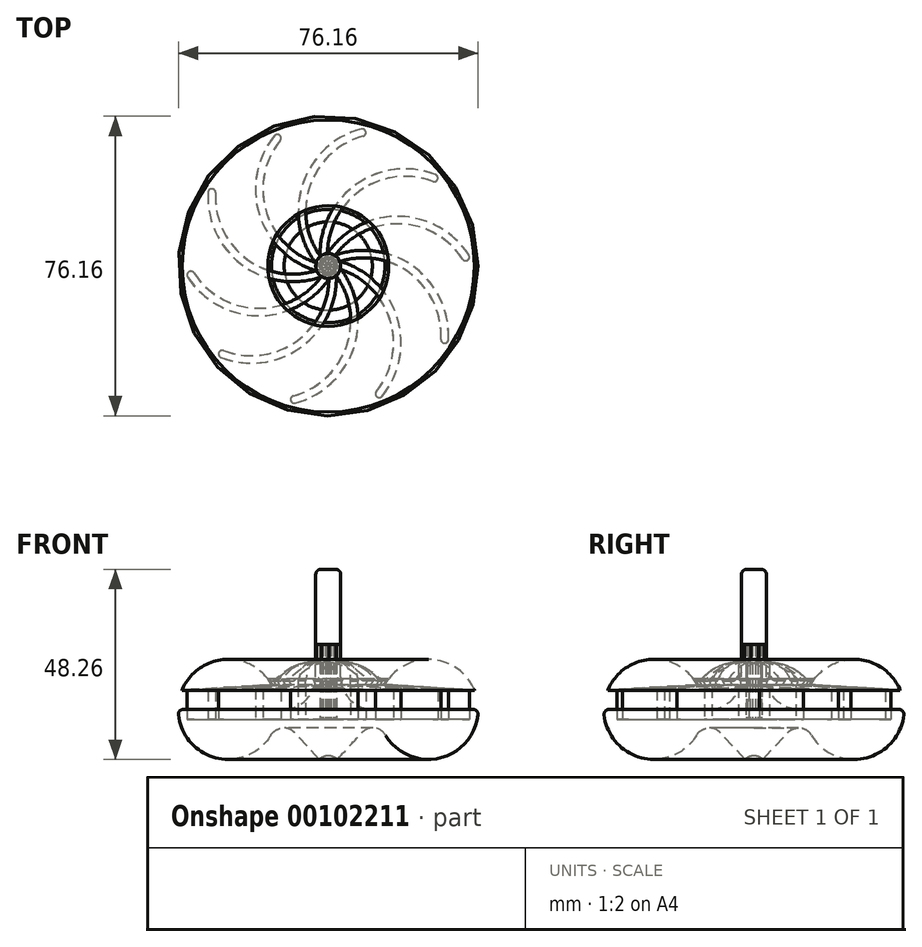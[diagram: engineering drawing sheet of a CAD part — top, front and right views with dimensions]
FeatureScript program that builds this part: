
annotation { "Feature Type Name" : "Feature", "Feature Type Description" : "" }
export const myFeature = defineFeature(function(context is Context, id is Id, definition is map)
    precondition{}
    {
        {
            var Q0;
            Q0=qCreatedBy(makeId("Front.planeOp"),FACE);
            var sketch = newSketch(context, id + "F0", { "sketchPlane" : qUnion([Q0])});
            skLineSegment(sketch, "E0", {"start": v(0, 50.8) * mm, "end": v(1.9, 50.8) * mm});
            skArc(sketch, "E1.trimOffspring", {"start": v(37.03, 20.46) * mm, "mid": v(26.9, 27.86) * mm, "end": v(15.35, 22.94) * mm});
            skLineSegment(sketch, "E2", {"start": v(16.06, 18.67) * mm, "end": v(35.87, 18.67) * mm});
            skLineSegment(sketch, "E3", {"start": v(3.17, 49.53) * mm, "end": v(3.17, 28.45) * mm});
            skArc(sketch, "E4.filletArc", {"start": v(3.17, 23.5) * mm, "mid": v(5.51, 17.73) * mm, "end": v(11.2, 15.24) * mm});
            skPoint(sketch, "E5.visualSharp", {"position": v(13.22, 18.67) * mm});
            skArc(sketch, "E5.filletArc", {"start": v(14.4, 21.52) * mm, "mid": v(14.42, 19.62) * mm, "end": v(16.06, 18.67) * mm});
            skPoint(sketch, "E6.visualSharp", {"position": v(37.68, 18.67) * mm});
            skArc(sketch, "E6.filletArc", {"start": v(35.87, 18.67) * mm, "mid": v(36.93, 19.25) * mm, "end": v(37.03, 20.46) * mm});
            skLineSegment(sketch, "E7", {"start": v(0, 50.8) * mm, "end": v(0, 3.43) * mm});
            skArc(sketch, "E8", {"start": v(14.58, 8.68) * mm, "mid": v(28.17, 2.83) * mm, "end": v(38.07, 13.83) * mm});
            skLineSegment(sketch, "E9", {"start": v(11.2, 15.24) * mm, "end": v(36.8, 15.24) * mm});
            skPoint(sketch, "E10.orphan", {"position": v(0, 10.8) * mm});
            skPoint(sketch, "E11.visualSharp", {"position": v(38.15, 15.24) * mm});
            skArc(sketch, "E11.filletArc", {"start": v(38.07, 13.83) * mm, "mid": v(37.75, 14.82) * mm, "end": v(36.8, 15.24) * mm});
            skLineSegment(sketch, "E12", {"start": v(2.33, 2.54) * mm, "end": v(8.5, 9.28) * mm});
            skPoint(sketch, "E13.orphan", {"position": v(13.97, 15.24) * mm});
            skPoint(sketch, "E14.visualSharp", {"position": v(12.81, 13.98) * mm});
            skArc(sketch, "E14.filletArc", {"start": v(14.58, 8.68) * mm, "mid": v(11.7, 10.5) * mm, "end": v(8.5, 9.28) * mm});
            skArc(sketch, "E15", {"start": v(13.38, 22.88) * mm, "mid": v(9.33, 25.96) * mm, "end": v(4.4, 27.18) * mm});
            skLineSegment(sketch, "E16", {"start": v(46.01, 43.83) * mm, "end": v(1.48, 42.53) * mm});
            skLineSegment(sketch, "E17", {"start": v(14.4, 21.52) * mm, "end": v(45.19, 19.62) * mm});
            skPoint(sketch, "E17.endSnap0", {"position": v(14.42, 19.62) * mm});
            skLineSegment(sketch, "E18", {"start": v(45.19, 19.62) * mm, "end": v(46.01, 43.83) * mm});
            skArc(sketch, "E19", {"start": v(2.3, 2.54) * mm, "mid": v(1.23, 3.2) * mm, "end": v(0, 3.43) * mm});
            skPoint(sketch, "E20.visualSharp", {"position": v(3.17, 50.8) * mm});
            skArc(sketch, "E20.filletArc", {"start": v(3.17, 49.53) * mm, "mid": v(2.8, 50.43) * mm, "end": v(1.9, 50.8) * mm});
            skArc(sketch, "E21.filletArc", {"start": v(3.17, 28.45) * mm, "mid": v(3.53, 27.57) * mm, "end": v(4.4, 27.18) * mm});
            skLineSegment(sketch, "E22", {"start": v(3.17, 23.5) * mm, "end": v(3.17, 28.45) * mm});
            skPoint(sketch, "E23.visualSharp", {"position": v(14.4, 21.52) * mm});
            skArc(sketch, "E23.filletArc", {"start": v(13.38, 22.88) * mm, "mid": v(14.38, 22.44) * mm, "end": v(15.35, 22.94) * mm});
            skLineSegment(sketch, "E24", {"start": v(15.35, 22.94) * mm, "end": v(14.4, 21.52) * mm});
            skLineSegment(sketch, "E25", {"start": v(2.33, 2.54) * mm, "end": v(2.3, 2.54) * mm});
            skSolve(sketch);
        }
        {
            var Q0;
            Q0=makeQuery(id+"F0.imprint","IMPRINT",FACE,{"disambiguationData":[TD([[makeQuery(id+"F0.imprint","IMPRINT",EDGE,{"derivedFrom":sQuery(id+"F0.wireOp",EDGE,"E0")}),-1.0]])]});
            var Q1;
            Q1=makeQuery(id+"F0.imprint","IMPRINT",FACE,{"disambiguationData":[TD([[makeQuery(id+"F0.imprint","IMPRINT",EDGE,{"derivedFrom":sQuery(id+"F0.wireOp",EDGE,"E1.trimOffspring")}),1.0]])]});
            var Q2;
            Q2=sQuery(id+"F0.wireOp",EDGE,"E7");
            revolve(context, id + "F1", {"entities" : qUnion([Q0, Q1]), "axis" : qUnion([Q2]), "revolveType" : RevolveType.FULL});
        }
        {
            var Q0;
            Q0=qCreatedBy(makeId("Top.planeOp"),FACE);
            var sketch = newSketch(context, id + "F2", { "sketchPlane" : qUnion([Q0])});
            skArc(sketch, "E26", {"start": v(8.37, 34.82) * mm, "mid": v(-6.96, 19.27) * mm, "end": v(-0.88, -1.7) * mm});
            skPoint(sketch, "E27.center", {"position": v(-0.53, 1.96) * mm});
            skArc(sketch, "E28.0", {"start": v(8.86, 32.98) * mm, "mid": v(-5.11, 18.8) * mm, "end": v(0.43, -0.32) * mm});
            skArc(sketch, "E29", {"start": v(8.86, 32.98) * mm, "mid": v(9.53, 34.15) * mm, "end": v(8.37, 34.82) * mm});
            skArc(sketch, "E30", {"start": v(-0.88, -1.7) * mm, "mid": v(0.46, -1.66) * mm, "end": v(0.43, -0.32) * mm});
            skSolve(sketch);
        }
        {
            var Q0;
            Q0=makeQuery(id+"F2.imprint","IMPRINT",FACE,{"disambiguationData":[TD([[makeQuery(id+"F2.imprint","IMPRINT",EDGE,{"derivedFrom":sQuery(id+"F2.wireOp",EDGE,"E26")}),1.0]])]});
            extrude(context, id + "F3", {"entities" : qUnion([Q0]), "depth" : 31.75 * mm, "hasSecondDirection" : true, "secondDirectionOppositeDirection" : false, "secondDirectionDepth" : 12.7 * mm});
        }
        {
            var Q0;
            Q0=makeQuery(id+"F3.opExtrude","SWEPT_BODY",BODY,{"disambiguationData":[OSD([sQuery(id+"F2.wireOp",EDGE,"E26"),sQuery(id+"F2.wireOp",EDGE,"E28.0"),sQuery(id+"F2.wireOp",EDGE,"E29"),sQuery(id+"F2.wireOp",EDGE,"E30")])]});
            var Q1;
            Q1=sQuery(id+"F0.wireOp",EDGE,"E7");
            circularPattern(context, id + "F4", {"entities" : qUnion([Q0]), "axis" : qUnion([Q1]), "angle" : 360 * degree, "instanceCount" : 10, "equalSpace" : true});
        }
        {
            var Q0;
            {var subQ0=sQuery(id+"F0.wireOp",EDGE,"E1.trimOffspring");Q0=makeQuery(id+"F0.imprint","IMPRINT",FACE,{"disambiguationData":[TD([[makeQuery(id+"F0.imprint","IMPRINT",EDGE,{"derivedFrom":subQ0}),1.0]])]});}
            var Q1;
            {var subQ1=sQuery(id+"F0.wireOp",EDGE,"E1.trimOffspring");Q1=makeQuery(id+"F0.imprint","IMPRINT",FACE,{"disambiguationData":[TD([[makeQuery(id+"F0.imprint","IMPRINT",EDGE,{"derivedFrom":subQ1}),-1.0]])]});}
            var Q2;
            Q2=sQuery(id+"F0.wireOp",EDGE,"E7");
            revolve(context, id + "F5", {"entities" : qUnion([Q0, Q1]), "axis" : qUnion([Q2]), "revolveType" : RevolveType.FULL});
        }
        {
            var Q0;
            Q0=makeQuery(id+"F5.opRevolve","SWEPT_BODY",BODY,{"disambiguationData":[OSD([sQuery(id+"F0.wireOp",EDGE,"E3"),sQuery(id+"F0.wireOp",EDGE,"E15"),sQuery(id+"F0.wireOp",EDGE,"E16"),sQuery(id+"F0.wireOp",EDGE,"E17"),sQuery(id+"F0.wireOp",EDGE,"E18")])]});
            var Q1;
            Q1=makeQuery(id+"F4.opPattern","COPY",BODY,{"derivedFrom":makeQuery(id+"F3.opExtrude","SWEPT_BODY",BODY,{"disambiguationData":[OSD([sQuery(id+"F2.wireOp",EDGE,"E26"),sQuery(id+"F2.wireOp",EDGE,"E28.0"),sQuery(id+"F2.wireOp",EDGE,"E29"),sQuery(id+"F2.wireOp",EDGE,"E30")])]}),"instanceName":"2"});
            var Q2;
            Q2=makeQuery(id+"F3.opExtrude","SWEPT_BODY",BODY,{"disambiguationData":[OSD([sQuery(id+"F2.wireOp",EDGE,"E26"),sQuery(id+"F2.wireOp",EDGE,"E28.0"),sQuery(id+"F2.wireOp",EDGE,"E29"),sQuery(id+"F2.wireOp",EDGE,"E30")])]});
            var Q3;
            Q3=makeQuery(id+"F4.opPattern","COPY",BODY,{"derivedFrom":makeQuery(id+"F3.opExtrude","SWEPT_BODY",BODY,{"disambiguationData":[OSD([sQuery(id+"F2.wireOp",EDGE,"E26"),sQuery(id+"F2.wireOp",EDGE,"E28.0"),sQuery(id+"F2.wireOp",EDGE,"E29"),sQuery(id+"F2.wireOp",EDGE,"E30")])]}),"instanceName":"1"});
            var Q4;
            Q4=makeQuery(id+"F4.opPattern","COPY",BODY,{"derivedFrom":makeQuery(id+"F3.opExtrude","SWEPT_BODY",BODY,{"disambiguationData":[OSD([sQuery(id+"F2.wireOp",EDGE,"E26"),sQuery(id+"F2.wireOp",EDGE,"E28.0"),sQuery(id+"F2.wireOp",EDGE,"E29"),sQuery(id+"F2.wireOp",EDGE,"E30")])]}),"instanceName":"3"});
            var Q5;
            Q5=makeQuery(id+"F4.opPattern","COPY",BODY,{"derivedFrom":makeQuery(id+"F3.opExtrude","SWEPT_BODY",BODY,{"disambiguationData":[OSD([sQuery(id+"F2.wireOp",EDGE,"E26"),sQuery(id+"F2.wireOp",EDGE,"E28.0"),sQuery(id+"F2.wireOp",EDGE,"E29"),sQuery(id+"F2.wireOp",EDGE,"E30")])]}),"instanceName":"4"});
            var Q6;
            Q6=makeQuery(id+"F4.opPattern","COPY",BODY,{"derivedFrom":makeQuery(id+"F3.opExtrude","SWEPT_BODY",BODY,{"disambiguationData":[OSD([sQuery(id+"F2.wireOp",EDGE,"E26"),sQuery(id+"F2.wireOp",EDGE,"E28.0"),sQuery(id+"F2.wireOp",EDGE,"E29"),sQuery(id+"F2.wireOp",EDGE,"E30")])]}),"instanceName":"5"});
            var Q7;
            Q7=makeQuery(id+"F4.opPattern","COPY",BODY,{"derivedFrom":makeQuery(id+"F3.opExtrude","SWEPT_BODY",BODY,{"disambiguationData":[OSD([sQuery(id+"F2.wireOp",EDGE,"E26"),sQuery(id+"F2.wireOp",EDGE,"E28.0"),sQuery(id+"F2.wireOp",EDGE,"E29"),sQuery(id+"F2.wireOp",EDGE,"E30")])]}),"instanceName":"6"});
            var Q8;
            Q8=makeQuery(id+"F4.opPattern","COPY",BODY,{"derivedFrom":makeQuery(id+"F3.opExtrude","SWEPT_BODY",BODY,{"disambiguationData":[OSD([sQuery(id+"F2.wireOp",EDGE,"E26"),sQuery(id+"F2.wireOp",EDGE,"E28.0"),sQuery(id+"F2.wireOp",EDGE,"E29"),sQuery(id+"F2.wireOp",EDGE,"E30")])]}),"instanceName":"7"});
            var Q9;
            Q9=makeQuery(id+"F4.opPattern","COPY",BODY,{"derivedFrom":makeQuery(id+"F3.opExtrude","SWEPT_BODY",BODY,{"disambiguationData":[OSD([sQuery(id+"F2.wireOp",EDGE,"E26"),sQuery(id+"F2.wireOp",EDGE,"E28.0"),sQuery(id+"F2.wireOp",EDGE,"E29"),sQuery(id+"F2.wireOp",EDGE,"E30")])]}),"instanceName":"8"});
            var Q10;
            Q10=makeQuery(id+"F4.opPattern","COPY",BODY,{"derivedFrom":makeQuery(id+"F3.opExtrude","SWEPT_BODY",BODY,{"disambiguationData":[OSD([sQuery(id+"F2.wireOp",EDGE,"E26"),sQuery(id+"F2.wireOp",EDGE,"E28.0"),sQuery(id+"F2.wireOp",EDGE,"E29"),sQuery(id+"F2.wireOp",EDGE,"E30")])]}),"instanceName":"9"});
            booleanBodies(context, id + "F6", {"operationType" : BooleanOperationType.SUBTRACTION, "tools" : qUnion([Q0]), "targets" : qUnion([Q1, Q2, Q3, Q4, Q5, Q6, Q7, Q8, Q9, Q10])});
        }
    });
